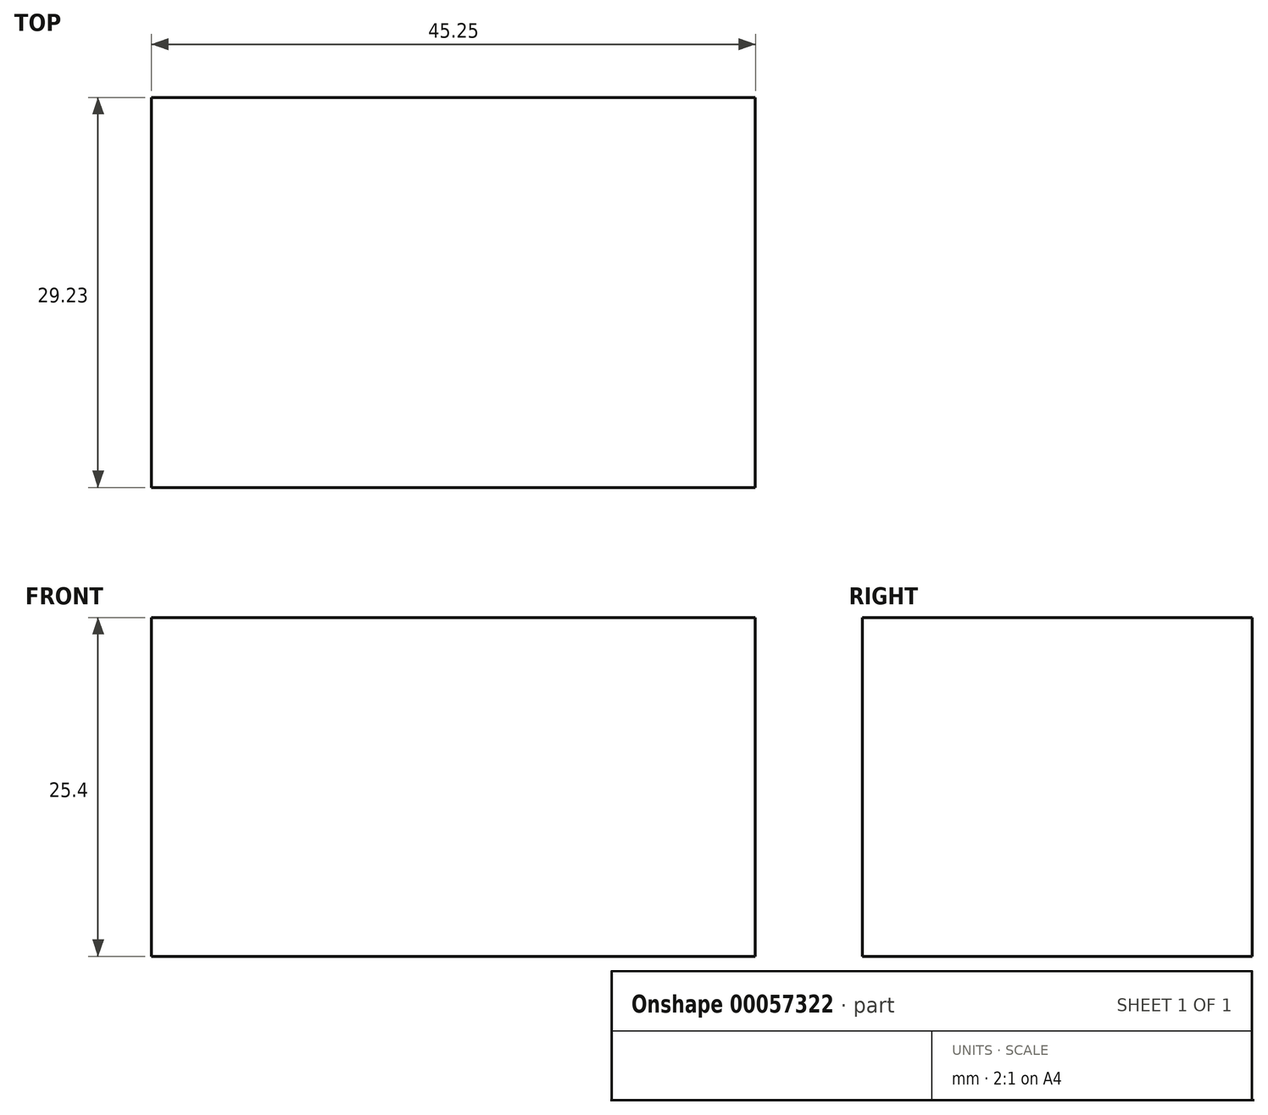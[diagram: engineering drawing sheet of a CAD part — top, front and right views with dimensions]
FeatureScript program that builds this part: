
annotation { "Feature Type Name" : "Feature", "Feature Type Description" : "" }
export const myFeature = defineFeature(function(context is Context, id is Id, definition is map)
    precondition{}
    {
        {
            var Q0;
            Q0=qCreatedBy(makeId("Top.planeOp"),FACE);
            var sketch = newSketch(context, id + "F0", { "sketchPlane" : qUnion([Q0])});
            skLineSegment(sketch, "E0.bottom", {"start": v(0, 0) * mm, "end": v(45.25, 0) * mm});
            skLineSegment(sketch, "E0.top", {"start": v(0, 29.23) * mm, "end": v(45.25, 29.23) * mm});
            skLineSegment(sketch, "E0.left", {"start": v(0, 0) * mm, "end": v(0, 29.23) * mm});
            skLineSegment(sketch, "E0.right", {"start": v(45.25, 0) * mm, "end": v(45.25, 29.23) * mm});
            skSolve(sketch);
        }
        {
            var Q0;
            Q0 = qSketchRegion(id + "F0", true);
            extrude(context, id + "F1", {"entities" : qUnion([Q0]), "depth" : 25.4 * mm});
        }
    });
